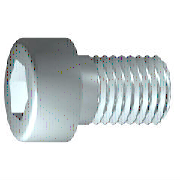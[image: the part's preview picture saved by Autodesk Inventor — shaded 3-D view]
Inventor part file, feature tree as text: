
AUTODESK INVENTOR PART (.ipt)
format: ipt  version: 2013 (Build 170138000, 138)  size: 182,784 bytes
history: native  units: mm (DEFAULTED — no unit token found)
features: sketch x2, extrude x1, plane x1
ambient origin geometry x7: Origin, YZ Plane, XY Plane, X Axis, Y Axis, Z Axis, Center Point
bodies: Solid1 (feature_tree), Body (feature_tree)
feature tree (4):
  extrude  "Slot"  Depth=0.276053mm
  plane  "Work Plane1"
  sketch  "Sketch1"  dims[d0=14.823948mm d1=0.276053mm]
  sketch  "Sketch2"  dims[d2=2.5mm d3=1.25mm d4=60.0deg d5=2.5mm d6=2.5mm d7=2.309401mm d8=4.5mm d10=90.0deg d11=10.0mm d9=0.0mm d12=14.823948mm d13=0.0mm d14=0.276052mm d15=0.276053mm d16=0.25mm d17=0.0mm d18=0.0mm d19=16.0mm d27=45.0deg d28=0.1mm d29=0.1mm]
